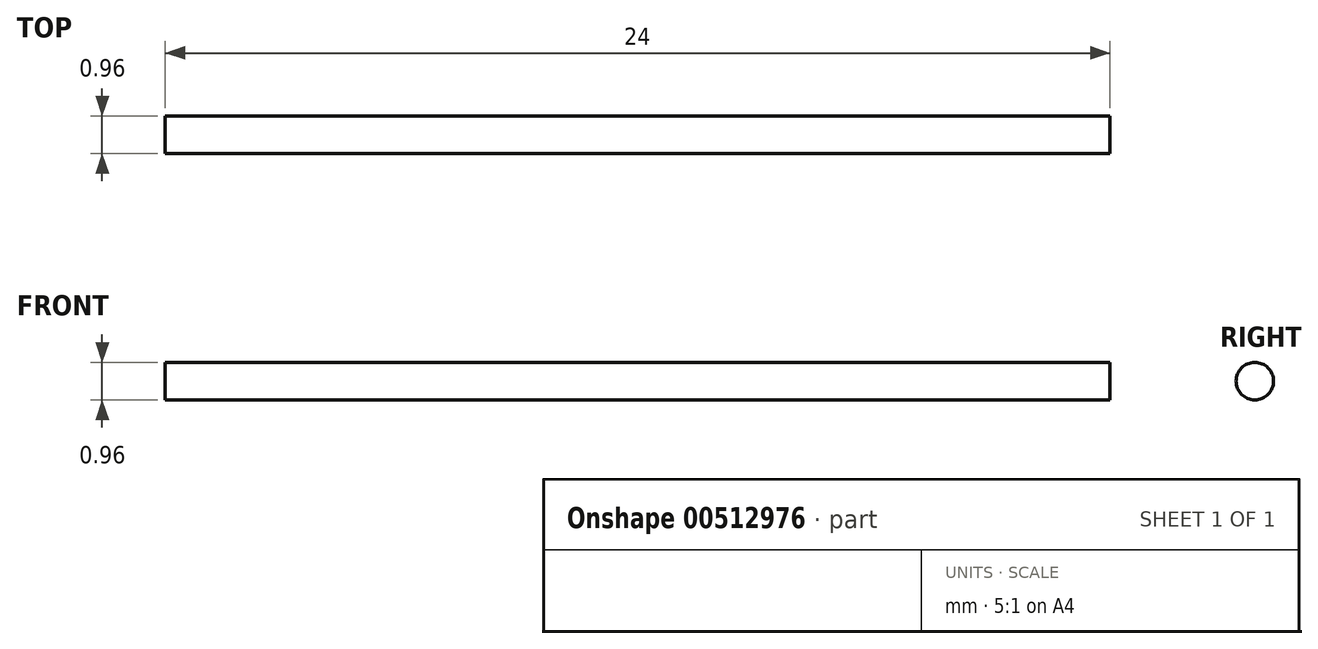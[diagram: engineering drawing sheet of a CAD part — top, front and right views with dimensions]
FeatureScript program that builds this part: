
annotation { "Feature Type Name" : "Feature", "Feature Type Description" : "" }
export const myFeature = defineFeature(function(context is Context, id is Id, definition is map)
    precondition{}
    {
        {
            var Q0;
            Q0=qCreatedBy(makeId("Right.planeOp"),FACE);
            var sketch = newSketch(context, id + "F0", { "sketchPlane" : qUnion([Q0])});
            skCircle(sketch, "E0", {"center": v(0, 0) * mm, "radius": 0.48 * mm});
            skSolve(sketch);
        }
        {
            var Q0;
            Q0 = qSketchRegion(id + "F0", true);
            extrude(context, id + "F1", {"entities" : qUnion([Q0]), "depth" : 12 * mm, "offsetDistance" : 25 * mm, "hasSecondDirection" : true, "secondDirectionOppositeDirection" : true, "secondDirectionDepth" : 12 * mm});
        }
    });
